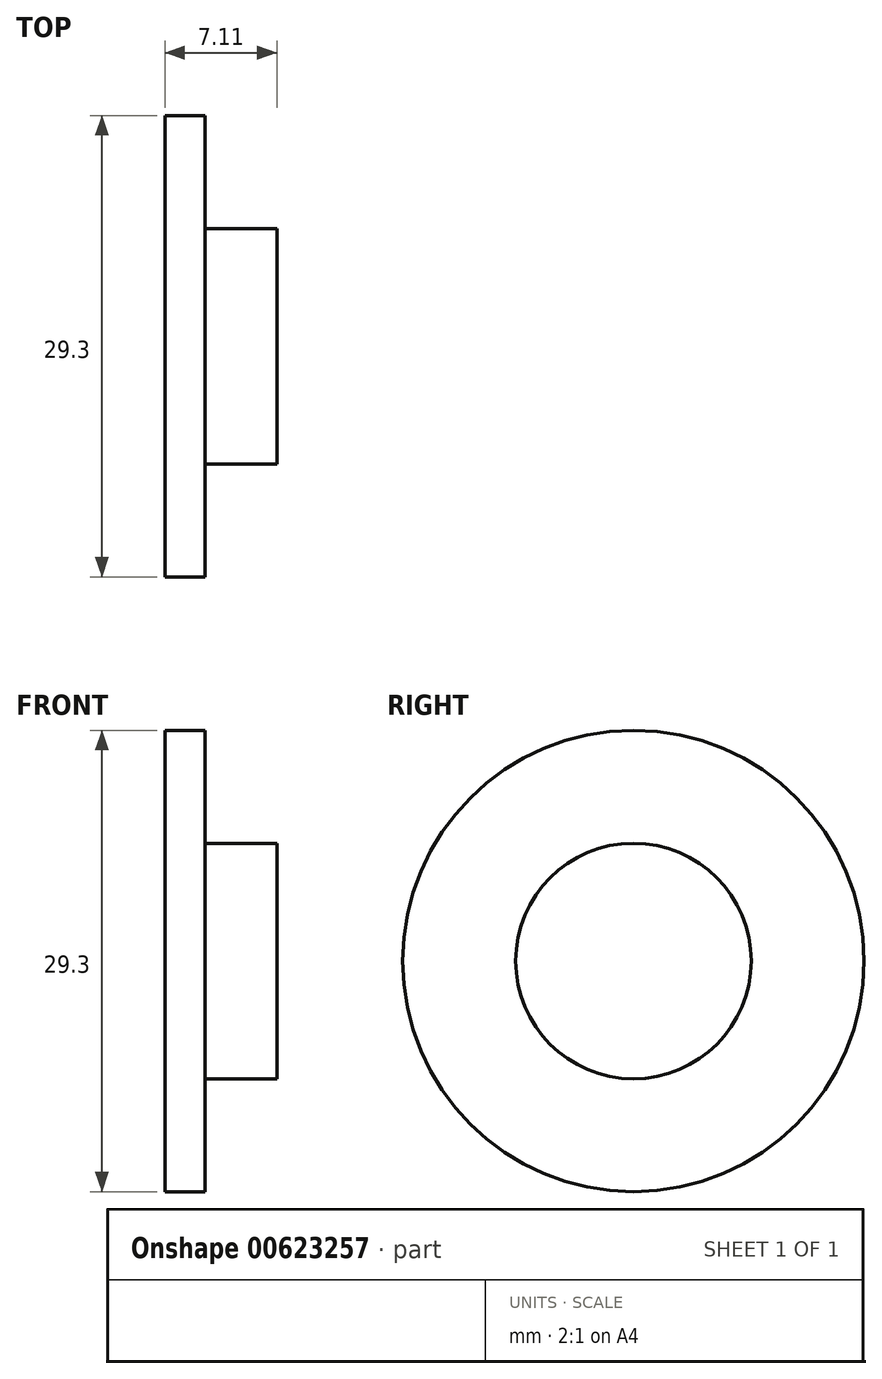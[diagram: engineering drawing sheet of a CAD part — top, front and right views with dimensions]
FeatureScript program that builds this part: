
annotation { "Feature Type Name" : "Feature", "Feature Type Description" : "" }
export const myFeature = defineFeature(function(context is Context, id is Id, definition is map)
    precondition{}
    {
        {
            var Q0;
            Q0=qCreatedBy(makeId("Right.planeOp"),FACE);
            var sketch = newSketch(context, id + "F0", { "sketchPlane" : qUnion([Q0])});
            skCircle(sketch, "E0", {"center": v(0, 0) * mm, "radius": 14.65 * mm});
            skSolve(sketch);
        }
        {
            var Q0;
            Q0 = qSketchRegion(id + "F0", true);
            extrude(context, id + "F1", {"entities" : qUnion([Q0]), "depth" : 2.54 * mm, "offsetDistance" : 25.4 * mm});
        }
        {
            var Q0;
            Q0=qCreatedBy(makeId("Right.planeOp"),FACE);
            var sketch = newSketch(context, id + "F2", { "sketchPlane" : qUnion([Q0])});
            skCircle(sketch, "E1", {"center": v(0, 0) * mm, "radius": 7.48 * mm});
            skSolve(sketch);
        }
        {
            var Q0;
            Q0 = qSketchRegion(id + "F2", true);
            extrude(context, id + "F3", {"entities" : qUnion([Q0]), "operationType" : NewBodyOperationType.ADD, "depth" : 7.11 * mm, "offsetDistance" : 25.4 * mm});
        }
    });
